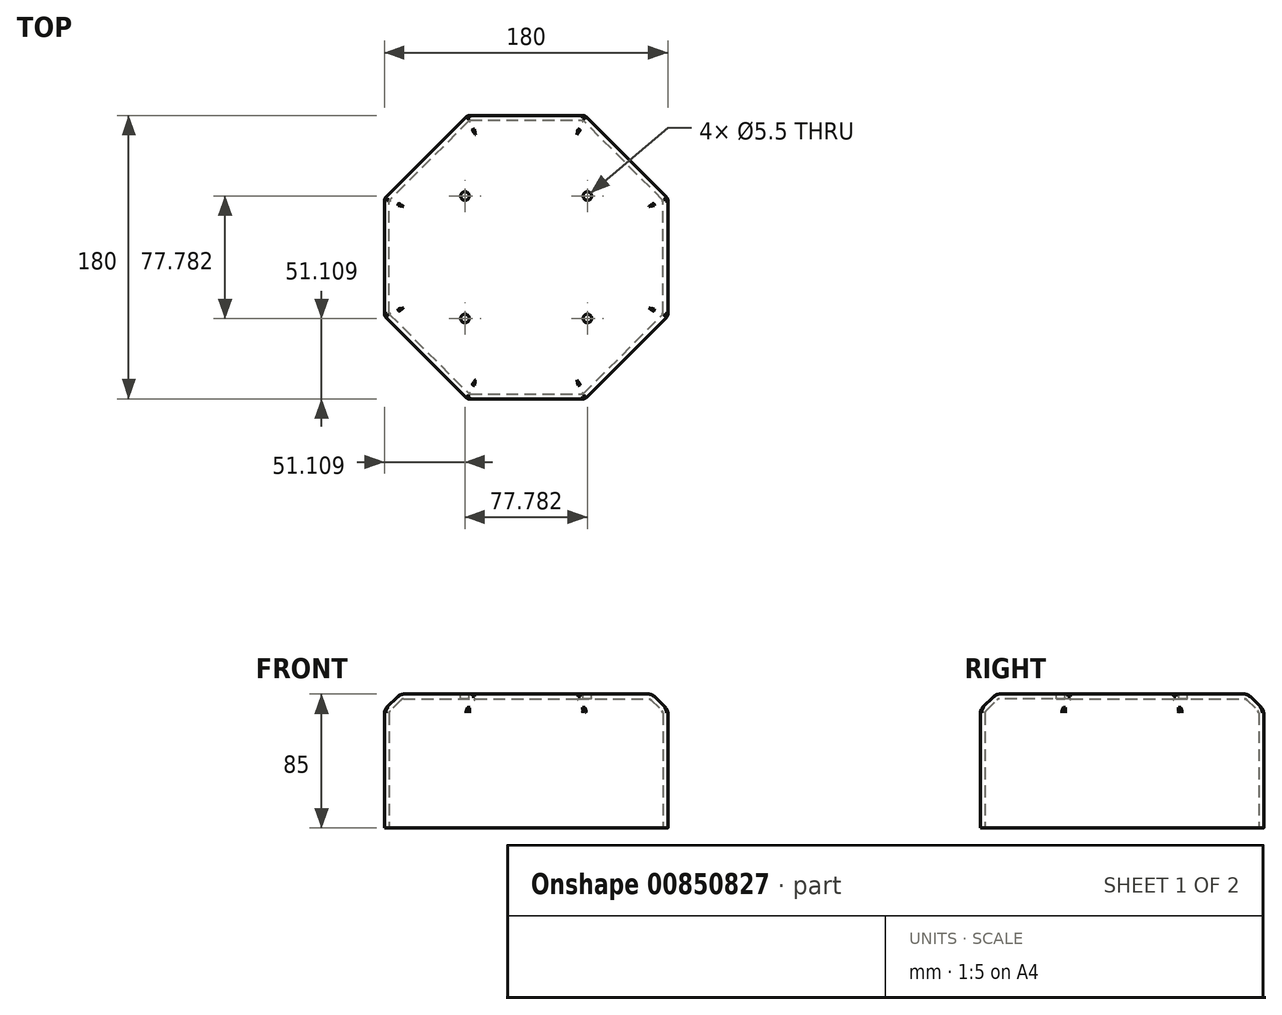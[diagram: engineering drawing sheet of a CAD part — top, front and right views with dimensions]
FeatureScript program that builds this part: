
annotation { "Feature Type Name" : "Feature", "Feature Type Description" : "" }
export const myFeature = defineFeature(function(context is Context, id is Id, definition is map)
    precondition{}
    {
        {
            var Q0;
            Q0=qCreatedBy(makeId("Top.planeOp"),FACE);
            var sketch = newSketch(context, id + "F0", { "sketchPlane" : qUnion([Q0])});
            skCircle(sketch, "E0.cCircle", {"center": v(0, 0) * mm, "radius": 90 * mm, "construction": true});
            skLineSegment(sketch, "E0.0", {"start": v(-37.28, 90) * mm, "end": v(37.28, 90) * mm});
            skLineSegment(sketch, "E0.1", {"start": v(37.28, 90) * mm, "end": v(90, 37.28) * mm});
            skLineSegment(sketch, "E0.2", {"start": v(90, 37.28) * mm, "end": v(90, -37.28) * mm});
            skLineSegment(sketch, "E0.3", {"start": v(90, -37.28) * mm, "end": v(37.28, -90) * mm});
            skLineSegment(sketch, "E0.4", {"start": v(37.28, -90) * mm, "end": v(-37.28, -90) * mm});
            skLineSegment(sketch, "E0.5", {"start": v(-37.28, -90) * mm, "end": v(-90, -37.28) * mm});
            skLineSegment(sketch, "E0.6", {"start": v(-90, -37.28) * mm, "end": v(-90, 37.28) * mm});
            skLineSegment(sketch, "E0.7", {"start": v(-90, 37.28) * mm, "end": v(-37.28, 90) * mm});
            skPoint(sketch, "E0.0.midPoint", {"position": v(0, 90) * mm});
            skSolve(sketch);
        }
        {
            var Q0;
            Q0 = qSketchRegion(id + "F0", true);
            extrude(context, id + "F1", {"entities" : qUnion([Q0]), "depth" : 25 * mm, "offsetDistance" : 25 * mm});
        }
        {
            var Q0;
            Q0=makeQuery(id+"F1.opExtrude","CAP_EDGE",EDGE,{"disambiguationData":[OSD([sQuery(id+"F0.wireOp",EDGE,"E0.5")])],"isStart":false});
            var Q1;
            Q1=makeQuery(id+"F1.opExtrude","CAP_EDGE",EDGE,{"disambiguationData":[OSD([sQuery(id+"F0.wireOp",EDGE,"E0.4")])],"isStart":false});
            var Q2;
            Q2=makeQuery(id+"F1.opExtrude","CAP_EDGE",EDGE,{"disambiguationData":[OSD([sQuery(id+"F0.wireOp",EDGE,"E0.3")])],"isStart":false});
            var Q3;
            Q3=makeQuery(id+"F1.opExtrude","CAP_EDGE",EDGE,{"disambiguationData":[OSD([sQuery(id+"F0.wireOp",EDGE,"E0.2")])],"isStart":false});
            var Q4;
            Q4=makeQuery(id+"F1.opExtrude","CAP_EDGE",EDGE,{"disambiguationData":[OSD([sQuery(id+"F0.wireOp",EDGE,"E0.1")])],"isStart":false});
            var Q5;
            Q5=makeQuery(id+"F1.opExtrude","CAP_EDGE",EDGE,{"disambiguationData":[OSD([sQuery(id+"F0.wireOp",EDGE,"E0.0")])],"isStart":false});
            var Q6;
            Q6=makeQuery(id+"F1.opExtrude","CAP_EDGE",EDGE,{"disambiguationData":[OSD([sQuery(id+"F0.wireOp",EDGE,"E0.7")])],"isStart":false});
            var Q7;
            Q7=makeQuery(id+"F1.opExtrude","CAP_EDGE",EDGE,{"disambiguationData":[OSD([sQuery(id+"F0.wireOp",EDGE,"E0.6")])],"isStart":false});
            chamfer(context, id + "F2", {"entities" : qUnion([Q0, Q1, Q2, Q3, Q4, Q5, Q6, Q7]), "width" : 10 * mm, "tangentPropagation" : true});
        }
        {
            var Q0;
            {var subQ0=sQuery(id+"F0.wireOp",EDGE,"E0.4");Q0=makeQuery(id+"F2.opChamfer","BLEND_EDGE",EDGE,{"blendedFrom":[makeQuery(id+"F1.opExtrude","CAP_EDGE",EDGE,{"disambiguationData":[OSD([subQ0])],"isStart":false}),makeQuery(id+"F1.opExtrude","SWEPT_FACE",FACE,{"disambiguationData":[OSD([subQ0])]})],"blendedInto":[makeQuery(id+"F1.opExtrude","SWEPT_FACE",FACE,{"disambiguationData":[OSD([subQ0])]})]});}
            var Q1;
            {var subQ0=sQuery(id+"F0.wireOp",EDGE,"E0.4");Q1=makeQuery(id+"F2.opChamfer","BLEND_EDGE",EDGE,{"blendedFrom":[makeQuery(id+"F1.opExtrude","CAP_EDGE",EDGE,{"disambiguationData":[OSD([subQ0])],"isStart":false}),makeQuery(id+"F1.opExtrude","CAP_FACE",FACE,{"disambiguationData":[OSD([sQuery(id+"F0.wireOp",EDGE,"E0.0"),sQuery(id+"F0.wireOp",EDGE,"E0.1"),sQuery(id+"F0.wireOp",EDGE,"E0.2"),sQuery(id+"F0.wireOp",EDGE,"E0.3"),subQ0,sQuery(id+"F0.wireOp",EDGE,"E0.5"),sQuery(id+"F0.wireOp",EDGE,"E0.6"),sQuery(id+"F0.wireOp",EDGE,"E0.7")])],"isStart":false})],"blendedInto":[makeQuery(id+"F1.opExtrude","CAP_FACE",FACE,{"disambiguationData":[OSD([sQuery(id+"F0.wireOp",EDGE,"E0.0"),sQuery(id+"F0.wireOp",EDGE,"E0.1"),sQuery(id+"F0.wireOp",EDGE,"E0.2"),sQuery(id+"F0.wireOp",EDGE,"E0.3"),subQ0,sQuery(id+"F0.wireOp",EDGE,"E0.5"),sQuery(id+"F0.wireOp",EDGE,"E0.6"),sQuery(id+"F0.wireOp",EDGE,"E0.7")])],"isStart":false})]});}
            var Q2;
            {var subQ0=sQuery(id+"F0.wireOp",EDGE,"E0.3");Q2=makeQuery(id+"F2.opChamfer","BLEND_EDGE",EDGE,{"blendedFrom":[makeQuery(id+"F1.opExtrude","CAP_EDGE",EDGE,{"disambiguationData":[OSD([subQ0])],"isStart":false}),makeQuery(id+"F1.opExtrude","CAP_FACE",FACE,{"disambiguationData":[OSD([sQuery(id+"F0.wireOp",EDGE,"E0.0"),sQuery(id+"F0.wireOp",EDGE,"E0.1"),sQuery(id+"F0.wireOp",EDGE,"E0.2"),subQ0,sQuery(id+"F0.wireOp",EDGE,"E0.4"),sQuery(id+"F0.wireOp",EDGE,"E0.5"),sQuery(id+"F0.wireOp",EDGE,"E0.6"),sQuery(id+"F0.wireOp",EDGE,"E0.7")])],"isStart":false})],"blendedInto":[makeQuery(id+"F1.opExtrude","CAP_FACE",FACE,{"disambiguationData":[OSD([sQuery(id+"F0.wireOp",EDGE,"E0.0"),sQuery(id+"F0.wireOp",EDGE,"E0.1"),sQuery(id+"F0.wireOp",EDGE,"E0.2"),subQ0,sQuery(id+"F0.wireOp",EDGE,"E0.4"),sQuery(id+"F0.wireOp",EDGE,"E0.5"),sQuery(id+"F0.wireOp",EDGE,"E0.6"),sQuery(id+"F0.wireOp",EDGE,"E0.7")])],"isStart":false})]});}
            var Q3;
            {var subQ0=sQuery(id+"F0.wireOp",EDGE,"E0.3");Q3=makeQuery(id+"F2.opChamfer","BLEND_EDGE",EDGE,{"blendedFrom":[makeQuery(id+"F1.opExtrude","CAP_EDGE",EDGE,{"disambiguationData":[OSD([subQ0])],"isStart":false}),makeQuery(id+"F1.opExtrude","SWEPT_FACE",FACE,{"disambiguationData":[OSD([subQ0])]})],"blendedInto":[makeQuery(id+"F1.opExtrude","SWEPT_FACE",FACE,{"disambiguationData":[OSD([subQ0])]})]});}
            var Q4;
            {var subQ0=sQuery(id+"F0.wireOp",EDGE,"E0.2");Q4=makeQuery(id+"F2.opChamfer","BLEND_EDGE",EDGE,{"blendedFrom":[makeQuery(id+"F1.opExtrude","CAP_EDGE",EDGE,{"disambiguationData":[OSD([subQ0])],"isStart":false}),makeQuery(id+"F1.opExtrude","CAP_FACE",FACE,{"disambiguationData":[OSD([sQuery(id+"F0.wireOp",EDGE,"E0.0"),sQuery(id+"F0.wireOp",EDGE,"E0.1"),subQ0,sQuery(id+"F0.wireOp",EDGE,"E0.3"),sQuery(id+"F0.wireOp",EDGE,"E0.4"),sQuery(id+"F0.wireOp",EDGE,"E0.5"),sQuery(id+"F0.wireOp",EDGE,"E0.6"),sQuery(id+"F0.wireOp",EDGE,"E0.7")])],"isStart":false})],"blendedInto":[makeQuery(id+"F1.opExtrude","CAP_FACE",FACE,{"disambiguationData":[OSD([sQuery(id+"F0.wireOp",EDGE,"E0.0"),sQuery(id+"F0.wireOp",EDGE,"E0.1"),subQ0,sQuery(id+"F0.wireOp",EDGE,"E0.3"),sQuery(id+"F0.wireOp",EDGE,"E0.4"),sQuery(id+"F0.wireOp",EDGE,"E0.5"),sQuery(id+"F0.wireOp",EDGE,"E0.6"),sQuery(id+"F0.wireOp",EDGE,"E0.7")])],"isStart":false})]});}
            var Q5;
            {var subQ0=sQuery(id+"F0.wireOp",EDGE,"E0.2");Q5=makeQuery(id+"F2.opChamfer","BLEND_EDGE",EDGE,{"blendedFrom":[makeQuery(id+"F1.opExtrude","CAP_EDGE",EDGE,{"disambiguationData":[OSD([subQ0])],"isStart":false}),makeQuery(id+"F1.opExtrude","SWEPT_FACE",FACE,{"disambiguationData":[OSD([subQ0])]})],"blendedInto":[makeQuery(id+"F1.opExtrude","SWEPT_FACE",FACE,{"disambiguationData":[OSD([subQ0])]})]});}
            var Q6;
            {var subQ0=sQuery(id+"F0.wireOp",EDGE,"E0.1");Q6=makeQuery(id+"F2.opChamfer","BLEND_EDGE",EDGE,{"blendedFrom":[makeQuery(id+"F1.opExtrude","CAP_EDGE",EDGE,{"disambiguationData":[OSD([subQ0])],"isStart":false}),makeQuery(id+"F1.opExtrude","CAP_FACE",FACE,{"disambiguationData":[OSD([sQuery(id+"F0.wireOp",EDGE,"E0.0"),subQ0,sQuery(id+"F0.wireOp",EDGE,"E0.2"),sQuery(id+"F0.wireOp",EDGE,"E0.3"),sQuery(id+"F0.wireOp",EDGE,"E0.4"),sQuery(id+"F0.wireOp",EDGE,"E0.5"),sQuery(id+"F0.wireOp",EDGE,"E0.6"),sQuery(id+"F0.wireOp",EDGE,"E0.7")])],"isStart":false})],"blendedInto":[makeQuery(id+"F1.opExtrude","CAP_FACE",FACE,{"disambiguationData":[OSD([sQuery(id+"F0.wireOp",EDGE,"E0.0"),subQ0,sQuery(id+"F0.wireOp",EDGE,"E0.2"),sQuery(id+"F0.wireOp",EDGE,"E0.3"),sQuery(id+"F0.wireOp",EDGE,"E0.4"),sQuery(id+"F0.wireOp",EDGE,"E0.5"),sQuery(id+"F0.wireOp",EDGE,"E0.6"),sQuery(id+"F0.wireOp",EDGE,"E0.7")])],"isStart":false})]});}
            var Q7;
            {var subQ0=sQuery(id+"F0.wireOp",EDGE,"E0.1");Q7=makeQuery(id+"F2.opChamfer","BLEND_EDGE",EDGE,{"blendedFrom":[makeQuery(id+"F1.opExtrude","CAP_EDGE",EDGE,{"disambiguationData":[OSD([subQ0])],"isStart":false}),makeQuery(id+"F1.opExtrude","SWEPT_FACE",FACE,{"disambiguationData":[OSD([subQ0])]})],"blendedInto":[makeQuery(id+"F1.opExtrude","SWEPT_FACE",FACE,{"disambiguationData":[OSD([subQ0])]})]});}
            var Q8;
            {var subQ0=sQuery(id+"F0.wireOp",EDGE,"E0.0");Q8=makeQuery(id+"F2.opChamfer","BLEND_EDGE",EDGE,{"blendedFrom":[makeQuery(id+"F1.opExtrude","CAP_EDGE",EDGE,{"disambiguationData":[OSD([subQ0])],"isStart":false}),makeQuery(id+"F1.opExtrude","CAP_FACE",FACE,{"disambiguationData":[OSD([subQ0,sQuery(id+"F0.wireOp",EDGE,"E0.1"),sQuery(id+"F0.wireOp",EDGE,"E0.2"),sQuery(id+"F0.wireOp",EDGE,"E0.3"),sQuery(id+"F0.wireOp",EDGE,"E0.4"),sQuery(id+"F0.wireOp",EDGE,"E0.5"),sQuery(id+"F0.wireOp",EDGE,"E0.6"),sQuery(id+"F0.wireOp",EDGE,"E0.7")])],"isStart":false})],"blendedInto":[makeQuery(id+"F1.opExtrude","CAP_FACE",FACE,{"disambiguationData":[OSD([subQ0,sQuery(id+"F0.wireOp",EDGE,"E0.1"),sQuery(id+"F0.wireOp",EDGE,"E0.2"),sQuery(id+"F0.wireOp",EDGE,"E0.3"),sQuery(id+"F0.wireOp",EDGE,"E0.4"),sQuery(id+"F0.wireOp",EDGE,"E0.5"),sQuery(id+"F0.wireOp",EDGE,"E0.6"),sQuery(id+"F0.wireOp",EDGE,"E0.7")])],"isStart":false})]});}
            var Q9;
            {var subQ0=sQuery(id+"F0.wireOp",EDGE,"E0.0");Q9=makeQuery(id+"F2.opChamfer","BLEND_EDGE",EDGE,{"blendedFrom":[makeQuery(id+"F1.opExtrude","CAP_EDGE",EDGE,{"disambiguationData":[OSD([subQ0])],"isStart":false}),makeQuery(id+"F1.opExtrude","SWEPT_FACE",FACE,{"disambiguationData":[OSD([subQ0])]})],"blendedInto":[makeQuery(id+"F1.opExtrude","SWEPT_FACE",FACE,{"disambiguationData":[OSD([subQ0])]})]});}
            var Q10;
            {var subQ0=sQuery(id+"F0.wireOp",EDGE,"E0.7");Q10=makeQuery(id+"F2.opChamfer","BLEND_EDGE",EDGE,{"blendedFrom":[makeQuery(id+"F1.opExtrude","CAP_EDGE",EDGE,{"disambiguationData":[OSD([subQ0])],"isStart":false}),makeQuery(id+"F1.opExtrude","CAP_FACE",FACE,{"disambiguationData":[OSD([sQuery(id+"F0.wireOp",EDGE,"E0.0"),sQuery(id+"F0.wireOp",EDGE,"E0.1"),sQuery(id+"F0.wireOp",EDGE,"E0.2"),sQuery(id+"F0.wireOp",EDGE,"E0.3"),sQuery(id+"F0.wireOp",EDGE,"E0.4"),sQuery(id+"F0.wireOp",EDGE,"E0.5"),sQuery(id+"F0.wireOp",EDGE,"E0.6"),subQ0])],"isStart":false})],"blendedInto":[makeQuery(id+"F1.opExtrude","CAP_FACE",FACE,{"disambiguationData":[OSD([sQuery(id+"F0.wireOp",EDGE,"E0.0"),sQuery(id+"F0.wireOp",EDGE,"E0.1"),sQuery(id+"F0.wireOp",EDGE,"E0.2"),sQuery(id+"F0.wireOp",EDGE,"E0.3"),sQuery(id+"F0.wireOp",EDGE,"E0.4"),sQuery(id+"F0.wireOp",EDGE,"E0.5"),sQuery(id+"F0.wireOp",EDGE,"E0.6"),subQ0])],"isStart":false})]});}
            var Q11;
            {var subQ0=sQuery(id+"F0.wireOp",EDGE,"E0.7");Q11=makeQuery(id+"F2.opChamfer","BLEND_EDGE",EDGE,{"blendedFrom":[makeQuery(id+"F1.opExtrude","CAP_EDGE",EDGE,{"disambiguationData":[OSD([subQ0])],"isStart":false}),makeQuery(id+"F1.opExtrude","SWEPT_FACE",FACE,{"disambiguationData":[OSD([subQ0])]})],"blendedInto":[makeQuery(id+"F1.opExtrude","SWEPT_FACE",FACE,{"disambiguationData":[OSD([subQ0])]})]});}
            var Q12;
            {var subQ0=sQuery(id+"F0.wireOp",EDGE,"E0.6");Q12=makeQuery(id+"F2.opChamfer","BLEND_EDGE",EDGE,{"blendedFrom":[makeQuery(id+"F1.opExtrude","CAP_EDGE",EDGE,{"disambiguationData":[OSD([subQ0])],"isStart":false}),makeQuery(id+"F1.opExtrude","SWEPT_FACE",FACE,{"disambiguationData":[OSD([subQ0])]})],"blendedInto":[makeQuery(id+"F1.opExtrude","SWEPT_FACE",FACE,{"disambiguationData":[OSD([subQ0])]})]});}
            var Q13;
            {var subQ0=sQuery(id+"F0.wireOp",EDGE,"E0.6");Q13=makeQuery(id+"F2.opChamfer","BLEND_EDGE",EDGE,{"blendedFrom":[makeQuery(id+"F1.opExtrude","CAP_EDGE",EDGE,{"disambiguationData":[OSD([subQ0])],"isStart":false}),makeQuery(id+"F1.opExtrude","CAP_FACE",FACE,{"disambiguationData":[OSD([sQuery(id+"F0.wireOp",EDGE,"E0.0"),sQuery(id+"F0.wireOp",EDGE,"E0.1"),sQuery(id+"F0.wireOp",EDGE,"E0.2"),sQuery(id+"F0.wireOp",EDGE,"E0.3"),sQuery(id+"F0.wireOp",EDGE,"E0.4"),sQuery(id+"F0.wireOp",EDGE,"E0.5"),subQ0,sQuery(id+"F0.wireOp",EDGE,"E0.7")])],"isStart":false})],"blendedInto":[makeQuery(id+"F1.opExtrude","CAP_FACE",FACE,{"disambiguationData":[OSD([sQuery(id+"F0.wireOp",EDGE,"E0.0"),sQuery(id+"F0.wireOp",EDGE,"E0.1"),sQuery(id+"F0.wireOp",EDGE,"E0.2"),sQuery(id+"F0.wireOp",EDGE,"E0.3"),sQuery(id+"F0.wireOp",EDGE,"E0.4"),sQuery(id+"F0.wireOp",EDGE,"E0.5"),subQ0,sQuery(id+"F0.wireOp",EDGE,"E0.7")])],"isStart":false})]});}
            var Q14;
            {var subQ0=sQuery(id+"F0.wireOp",EDGE,"E0.5");Q14=makeQuery(id+"F2.opChamfer","BLEND_EDGE",EDGE,{"blendedFrom":[makeQuery(id+"F1.opExtrude","CAP_EDGE",EDGE,{"disambiguationData":[OSD([subQ0])],"isStart":false}),makeQuery(id+"F1.opExtrude","CAP_FACE",FACE,{"disambiguationData":[OSD([sQuery(id+"F0.wireOp",EDGE,"E0.0"),sQuery(id+"F0.wireOp",EDGE,"E0.1"),sQuery(id+"F0.wireOp",EDGE,"E0.2"),sQuery(id+"F0.wireOp",EDGE,"E0.3"),sQuery(id+"F0.wireOp",EDGE,"E0.4"),subQ0,sQuery(id+"F0.wireOp",EDGE,"E0.6"),sQuery(id+"F0.wireOp",EDGE,"E0.7")])],"isStart":false})],"blendedInto":[makeQuery(id+"F1.opExtrude","CAP_FACE",FACE,{"disambiguationData":[OSD([sQuery(id+"F0.wireOp",EDGE,"E0.0"),sQuery(id+"F0.wireOp",EDGE,"E0.1"),sQuery(id+"F0.wireOp",EDGE,"E0.2"),sQuery(id+"F0.wireOp",EDGE,"E0.3"),sQuery(id+"F0.wireOp",EDGE,"E0.4"),subQ0,sQuery(id+"F0.wireOp",EDGE,"E0.6"),sQuery(id+"F0.wireOp",EDGE,"E0.7")])],"isStart":false})]});}
            var Q15;
            {var subQ0=sQuery(id+"F0.wireOp",EDGE,"E0.5");Q15=makeQuery(id+"F2.opChamfer","BLEND_EDGE",EDGE,{"blendedFrom":[makeQuery(id+"F1.opExtrude","CAP_EDGE",EDGE,{"disambiguationData":[OSD([subQ0])],"isStart":false}),makeQuery(id+"F1.opExtrude","SWEPT_FACE",FACE,{"disambiguationData":[OSD([subQ0])]})],"blendedInto":[makeQuery(id+"F1.opExtrude","SWEPT_FACE",FACE,{"disambiguationData":[OSD([subQ0])]})]});}
            fillet(context, id + "F3", {"entities" : qUnion([Q0, Q1, Q2, Q3, Q4, Q5, Q6, Q7, Q8, Q9, Q10, Q11, Q12, Q13, Q14, Q15]), "radius" : 5 * mm, "tangentPropagation" : true, "allowEdgeOverflow" : false});
        }
        {
            var Q0;
            Q0=makeQuery(id+"F1.opExtrude","CAP_FACE",FACE,{"disambiguationData":[OSD([sQuery(id+"F0.wireOp",EDGE,"E0.0"),sQuery(id+"F0.wireOp",EDGE,"E0.1"),sQuery(id+"F0.wireOp",EDGE,"E0.2"),sQuery(id+"F0.wireOp",EDGE,"E0.3"),sQuery(id+"F0.wireOp",EDGE,"E0.4"),sQuery(id+"F0.wireOp",EDGE,"E0.5"),sQuery(id+"F0.wireOp",EDGE,"E0.6"),sQuery(id+"F0.wireOp",EDGE,"E0.7")])],"isStart":true});
            shell(context, id + "F4", {"entities" : qUnion([Q0]), "thickness" : 3 * mm});
        }
        {
            var Q0;
            Q0=makeQuery(id+"F1.opExtrude","CAP_FACE",FACE,{"disambiguationData":[OSD([sQuery(id+"F0.wireOp",EDGE,"E0.0"),sQuery(id+"F0.wireOp",EDGE,"E0.1"),sQuery(id+"F0.wireOp",EDGE,"E0.2"),sQuery(id+"F0.wireOp",EDGE,"E0.3"),sQuery(id+"F0.wireOp",EDGE,"E0.4"),sQuery(id+"F0.wireOp",EDGE,"E0.5"),sQuery(id+"F0.wireOp",EDGE,"E0.6"),sQuery(id+"F0.wireOp",EDGE,"E0.7")])],"isStart":false});
            var sketch = newSketch(context, id + "F5", { "sketchPlane" : qUnion([Q0])});
            skLineSegment(sketch, "E1", {"start": v(0, 0) * mm, "end": v(-56.57, 56.57) * mm, "construction": true});
            skCircle(sketch, "E2", {"center": v(-38.9, 38.9) * mm, "radius": 2.75 * mm});
            skCircle(sketch, "E3.1.0", {"center": v(-38.9, -38.9) * mm, "radius": 2.75 * mm});
            skCircle(sketch, "E3.2.0", {"center": v(38.9, -38.9) * mm, "radius": 2.75 * mm});
            skCircle(sketch, "E3.3.0", {"center": v(38.9, 38.9) * mm, "radius": 2.75 * mm});
            skPoint(sketch, "E3.center", {"position": v(0, 0) * mm});
            skSolve(sketch);
        }
        {
            var Q0;
            Q0 = qSketchRegion(id + "F5", true);
            extrude(context, id + "F6", {"entities" : qUnion([Q0]), "operationType" : NewBodyOperationType.REMOVE, "oppositeDirection" : true, "depth" : 25 * mm, "offsetDistance" : 25 * mm});
        }
        {
            var Q0;
            Q0=makeQuery(id+"F1.opExtrude","SWEPT_EDGE",EDGE,{"disambiguationData":[OSD([sQuery(id+"F0.wireOp",EDGE,"E0.4"),sQuery(id+"F0.wireOp",EDGE,"E0.5")])]});
            var Q1;
            Q1=makeQuery(id+"F1.opExtrude","SWEPT_EDGE",EDGE,{"disambiguationData":[OSD([sQuery(id+"F0.wireOp",EDGE,"E0.3"),sQuery(id+"F0.wireOp",EDGE,"E0.4")])]});
            var Q2;
            Q2=makeQuery(id+"F1.opExtrude","SWEPT_EDGE",EDGE,{"disambiguationData":[OSD([sQuery(id+"F0.wireOp",EDGE,"E0.2"),sQuery(id+"F0.wireOp",EDGE,"E0.3")])]});
            var Q3;
            Q3=makeQuery(id+"F1.opExtrude","SWEPT_EDGE",EDGE,{"disambiguationData":[OSD([sQuery(id+"F0.wireOp",EDGE,"E0.1"),sQuery(id+"F0.wireOp",EDGE,"E0.2")])]});
            var Q4;
            Q4=makeQuery(id+"F1.opExtrude","SWEPT_EDGE",EDGE,{"disambiguationData":[OSD([sQuery(id+"F0.wireOp",EDGE,"E0.5"),sQuery(id+"F0.wireOp",EDGE,"E0.6")])]});
            var Q5;
            Q5=makeQuery(id+"F1.opExtrude","SWEPT_EDGE",EDGE,{"disambiguationData":[OSD([sQuery(id+"F0.wireOp",EDGE,"E0.6"),sQuery(id+"F0.wireOp",EDGE,"E0.7")])]});
            var Q6;
            Q6=makeQuery(id+"F2.opChamfer","BLEND_EDGE",EDGE,{"blendedFrom":[makeQuery(id+"F1.opExtrude","CAP_EDGE",EDGE,{"disambiguationData":[OSD([sQuery(id+"F0.wireOp",EDGE,"E0.0")])],"isStart":false}),makeQuery(id+"F1.opExtrude","CAP_EDGE",EDGE,{"disambiguationData":[OSD([sQuery(id+"F0.wireOp",EDGE,"E0.7")])],"isStart":false})],"blendedInto":[]});
            var Q7;
            Q7=makeQuery(id+"F2.opChamfer","BLEND_EDGE",EDGE,{"blendedFrom":[makeQuery(id+"F1.opExtrude","CAP_EDGE",EDGE,{"disambiguationData":[OSD([sQuery(id+"F0.wireOp",EDGE,"E0.0")])],"isStart":false}),makeQuery(id+"F1.opExtrude","CAP_EDGE",EDGE,{"disambiguationData":[OSD([sQuery(id+"F0.wireOp",EDGE,"E0.1")])],"isStart":false})],"blendedInto":[]});
            fillet(context, id + "F7", {"entities" : qUnion([Q0, Q1, Q2, Q3, Q4, Q5, Q6, Q7]), "radius" : 3 * mm, "tangentPropagation" : true, "allowEdgeOverflow" : false});
        }
        {
            var Q0;
            Q0=makeQuery(id+"F1.opExtrude","CAP_FACE",FACE,{"disambiguationData":[OSD([sQuery(id+"F0.wireOp",EDGE,"E0.0"),sQuery(id+"F0.wireOp",EDGE,"E0.1"),sQuery(id+"F0.wireOp",EDGE,"E0.2"),sQuery(id+"F0.wireOp",EDGE,"E0.3"),sQuery(id+"F0.wireOp",EDGE,"E0.4"),sQuery(id+"F0.wireOp",EDGE,"E0.5"),sQuery(id+"F0.wireOp",EDGE,"E0.6"),sQuery(id+"F0.wireOp",EDGE,"E0.7")])],"isStart":true});
            var sketch = newSketch(context, id + "F8", { "sketchPlane" : qUnion([Q0])});
            skLineSegment(sketch, "E4.0", {"start": v(90, -36.04) * mm, "end": v(90, 36.04) * mm});
            skArc(sketch, "E4.1", {"start": v(90, 36.04) * mm, "mid": v(89.77, 37.18) * mm, "end": v(89.12, 38.16) * mm});
            skLineSegment(sketch, "E4.2", {"start": v(89.12, 38.16) * mm, "end": v(38.16, 89.12) * mm});
            skArc(sketch, "E4.3", {"start": v(38.16, 89.12) * mm, "mid": v(37.18, 89.77) * mm, "end": v(36.04, 90) * mm});
            skLineSegment(sketch, "E4.4", {"start": v(36.04, 90) * mm, "end": v(-36.04, 90) * mm});
            skPoint(sketch, "E4.5", {"position": v(-38.16, 89.12) * mm});
            skArc(sketch, "E4.6", {"start": v(-36.04, 90) * mm, "mid": v(-37.18, 89.77) * mm, "end": v(-38.16, 89.12) * mm});
            skLineSegment(sketch, "E4.7", {"start": v(-38.16, 89.12) * mm, "end": v(-89.12, 38.16) * mm});
            skArc(sketch, "E4.8", {"start": v(-89.12, 38.16) * mm, "mid": v(-89.77, 37.18) * mm, "end": v(-90, 36.04) * mm});
            skLineSegment(sketch, "E4.9", {"start": v(-90, 36.04) * mm, "end": v(-90, -36.04) * mm});
            skArc(sketch, "E4.10", {"start": v(-90, -36.04) * mm, "mid": v(-89.77, -37.18) * mm, "end": v(-89.12, -38.16) * mm});
            skLineSegment(sketch, "E4.11", {"start": v(-89.12, -38.16) * mm, "end": v(-38.16, -89.12) * mm});
            skArc(sketch, "E4.12", {"start": v(-38.16, -89.12) * mm, "mid": v(-37.18, -89.77) * mm, "end": v(-36.04, -90) * mm});
            skLineSegment(sketch, "E4.13", {"start": v(-36.04, -90) * mm, "end": v(36.04, -90) * mm});
            skArc(sketch, "E4.14", {"start": v(36.04, -90) * mm, "mid": v(37.18, -89.77) * mm, "end": v(38.16, -89.12) * mm});
            skLineSegment(sketch, "E4.15", {"start": v(38.16, -89.12) * mm, "end": v(89.12, -38.16) * mm});
            skArc(sketch, "E4.16", {"start": v(89.12, -38.16) * mm, "mid": v(89.77, -37.18) * mm, "end": v(90, -36.04) * mm});
            skPoint(sketch, "E4.17", {"position": v(89.77, 37.18) * mm});
            skLineSegment(sketch, "E5.0", {"start": v(36.04, 87) * mm, "end": v(-36.04, 87) * mm});
            skLineSegment(sketch, "E5.1", {"start": v(87, 36.04) * mm, "end": v(36.04, 87) * mm});
            skLineSegment(sketch, "E5.2", {"start": v(-36.04, 87) * mm, "end": v(-87, 36.04) * mm});
            skLineSegment(sketch, "E5.3", {"start": v(87, -36.04) * mm, "end": v(87, 36.04) * mm});
            skLineSegment(sketch, "E5.4", {"start": v(-87, 36.04) * mm, "end": v(-87, -36.04) * mm});
            skLineSegment(sketch, "E5.5", {"start": v(-87, -36.04) * mm, "end": v(-36.04, -87) * mm});
            skLineSegment(sketch, "E5.6", {"start": v(-36.04, -87) * mm, "end": v(36.04, -87) * mm});
            skLineSegment(sketch, "E5.7", {"start": v(36.04, -87) * mm, "end": v(87, -36.04) * mm});
            skSolve(sketch);
        }
        {
            var Q0;
            Q0 = qSketchRegion(id + "F8", true);
            extrude(context, id + "F9", {"entities" : qUnion([Q0]), "operationType" : NewBodyOperationType.ADD, "depth" : 60 * mm, "offsetDistance" : 25 * mm});
        }
        {
            var Q0;
            {var subQ0=sQuery(id+"F0.wireOp",EDGE,"E0.6");var subQ1=sQuery(id+"F0.wireOp",EDGE,"E0.5");Q0=makeQuery(id+"F9.boolean.opBoolean","MERGE",EDGE,{"derivedFrom":[makeQuery(id+"F4.opShell","OFFSET_EDGE",EDGE,{"disambiguationData":[OSD([subQ1,subQ0]),TDD([makeQuery(id+"F1.opExtrude","SWEPT_EDGE",EDGE,{"disambiguationData":[OSD([subQ1,subQ0])]})])]}),makeQuery(id+"F9.opExtrude","SWEPT_EDGE",EDGE,{"disambiguationData":[OSD([sQuery(id+"F8.wireOp",EDGE,"E5.2"),sQuery(id+"F8.wireOp",EDGE,"E5.4")])]})]});}
            var Q1;
            {var subQ0=sQuery(id+"F0.wireOp",EDGE,"E0.5");var subQ1=sQuery(id+"F0.wireOp",EDGE,"E0.4");Q1=makeQuery(id+"F9.boolean.opBoolean","MERGE",EDGE,{"derivedFrom":[makeQuery(id+"F4.opShell","OFFSET_EDGE",EDGE,{"disambiguationData":[OSD([subQ1,subQ0]),TDD([makeQuery(id+"F1.opExtrude","SWEPT_EDGE",EDGE,{"disambiguationData":[OSD([subQ1,subQ0])]})])]}),makeQuery(id+"F9.opExtrude","SWEPT_EDGE",EDGE,{"disambiguationData":[OSD([sQuery(id+"F8.wireOp",EDGE,"E5.0"),sQuery(id+"F8.wireOp",EDGE,"E5.2")])]})]});}
            var Q2;
            {var subQ0=sQuery(id+"F0.wireOp",EDGE,"E0.4");var subQ1=sQuery(id+"F0.wireOp",EDGE,"E0.3");Q2=makeQuery(id+"F9.boolean.opBoolean","MERGE",EDGE,{"derivedFrom":[makeQuery(id+"F4.opShell","OFFSET_EDGE",EDGE,{"disambiguationData":[OSD([subQ1,subQ0]),TDD([makeQuery(id+"F1.opExtrude","SWEPT_EDGE",EDGE,{"disambiguationData":[OSD([subQ1,subQ0])]})])]}),makeQuery(id+"F9.opExtrude","SWEPT_EDGE",EDGE,{"disambiguationData":[OSD([sQuery(id+"F8.wireOp",EDGE,"E5.0"),sQuery(id+"F8.wireOp",EDGE,"E5.1")])]})]});}
            var Q3;
            {var subQ0=sQuery(id+"F0.wireOp",EDGE,"E0.3");var subQ1=sQuery(id+"F0.wireOp",EDGE,"E0.2");Q3=makeQuery(id+"F9.boolean.opBoolean","MERGE",EDGE,{"derivedFrom":[makeQuery(id+"F4.opShell","OFFSET_EDGE",EDGE,{"disambiguationData":[OSD([subQ1,subQ0]),TDD([makeQuery(id+"F1.opExtrude","SWEPT_EDGE",EDGE,{"disambiguationData":[OSD([subQ1,subQ0])]})])]}),makeQuery(id+"F9.opExtrude","SWEPT_EDGE",EDGE,{"disambiguationData":[OSD([sQuery(id+"F8.wireOp",EDGE,"E5.1"),sQuery(id+"F8.wireOp",EDGE,"E5.3")])]})]});}
            var Q4;
            {var subQ0=sQuery(id+"F0.wireOp",EDGE,"E0.2");var subQ1=sQuery(id+"F0.wireOp",EDGE,"E0.1");Q4=makeQuery(id+"F9.boolean.opBoolean","MERGE",EDGE,{"derivedFrom":[makeQuery(id+"F4.opShell","OFFSET_EDGE",EDGE,{"disambiguationData":[OSD([subQ1,subQ0]),TDD([makeQuery(id+"F1.opExtrude","SWEPT_EDGE",EDGE,{"disambiguationData":[OSD([subQ1,subQ0])]})])]}),makeQuery(id+"F9.opExtrude","SWEPT_EDGE",EDGE,{"disambiguationData":[OSD([sQuery(id+"F8.wireOp",EDGE,"E5.3"),sQuery(id+"F8.wireOp",EDGE,"E5.7")])]})]});}
            var Q5;
            {var subQ0=sQuery(id+"F0.wireOp",EDGE,"E0.1");var subQ1=sQuery(id+"F0.wireOp",EDGE,"E0.0");Q5=makeQuery(id+"F9.boolean.opBoolean","MERGE",EDGE,{"derivedFrom":[makeQuery(id+"F4.opShell","OFFSET_EDGE",EDGE,{"disambiguationData":[OSD([subQ1,subQ0]),TDD([makeQuery(id+"F1.opExtrude","SWEPT_EDGE",EDGE,{"disambiguationData":[OSD([subQ1,subQ0])]})])]}),makeQuery(id+"F9.opExtrude","SWEPT_EDGE",EDGE,{"disambiguationData":[OSD([sQuery(id+"F8.wireOp",EDGE,"E5.6"),sQuery(id+"F8.wireOp",EDGE,"E5.7")])]})]});}
            var Q6;
            {var subQ0=sQuery(id+"F0.wireOp",EDGE,"E0.7");var subQ1=sQuery(id+"F0.wireOp",EDGE,"E0.0");Q6=makeQuery(id+"F9.boolean.opBoolean","MERGE",EDGE,{"derivedFrom":[makeQuery(id+"F4.opShell","OFFSET_EDGE",EDGE,{"disambiguationData":[OSD([subQ1,subQ0]),TDD([makeQuery(id+"F1.opExtrude","SWEPT_EDGE",EDGE,{"disambiguationData":[OSD([subQ1,subQ0])]})])]}),makeQuery(id+"F9.opExtrude","SWEPT_EDGE",EDGE,{"disambiguationData":[OSD([sQuery(id+"F8.wireOp",EDGE,"E5.5"),sQuery(id+"F8.wireOp",EDGE,"E5.6")])]})]});}
            var Q7;
            {var subQ0=sQuery(id+"F0.wireOp",EDGE,"E0.7");var subQ1=sQuery(id+"F0.wireOp",EDGE,"E0.6");Q7=makeQuery(id+"F9.boolean.opBoolean","MERGE",EDGE,{"derivedFrom":[makeQuery(id+"F4.opShell","OFFSET_EDGE",EDGE,{"disambiguationData":[OSD([subQ1,subQ0]),TDD([makeQuery(id+"F1.opExtrude","SWEPT_EDGE",EDGE,{"disambiguationData":[OSD([subQ1,subQ0])]})])]}),makeQuery(id+"F9.opExtrude","SWEPT_EDGE",EDGE,{"disambiguationData":[OSD([sQuery(id+"F8.wireOp",EDGE,"E5.4"),sQuery(id+"F8.wireOp",EDGE,"E5.5")])]})]});}
            fillet(context, id + "F10", {"entities" : qUnion([Q0, Q1, Q2, Q3, Q4, Q5, Q6, Q7]), "radius" : 1 * mm, "tangentPropagation" : true, "allowEdgeOverflow" : false});
        }
    });
